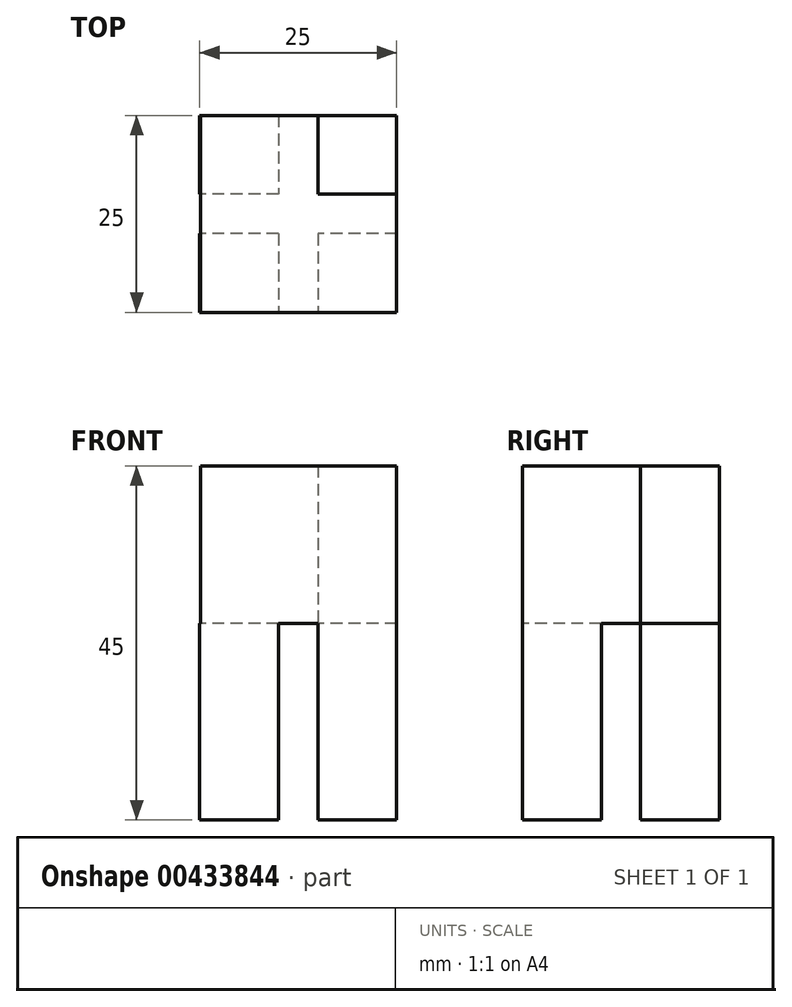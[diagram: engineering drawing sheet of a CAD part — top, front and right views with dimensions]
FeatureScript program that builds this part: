
annotation { "Feature Type Name" : "Feature", "Feature Type Description" : "" }
export const myFeature = defineFeature(function(context is Context, id is Id, definition is map)
    precondition{}
    {
        {
            var Q0;
            Q0=qCreatedBy(makeId("Top.planeOp"),FACE);
            var sketch = newSketch(context, id + "F0", { "sketchPlane" : qUnion([Q0])});
            skLineSegment(sketch, "E0.bottom", {"start": v(0, 0) * mm, "end": v(-10, 0) * mm});
            skLineSegment(sketch, "E0.top", {"start": v(0, -10) * mm, "end": v(-10, -10) * mm});
            skLineSegment(sketch, "E0.left", {"start": v(0, 0) * mm, "end": v(0, -10) * mm});
            skLineSegment(sketch, "E0.right", {"start": v(-10, 0) * mm, "end": v(-10, -10) * mm});
            skLineSegment(sketch, "E1.0.1.0", {"start": v(0, 15) * mm, "end": v(-10, 15) * mm});
            skLineSegment(sketch, "E1.0.1.1", {"start": v(-10, 15) * mm, "end": v(-10, 5) * mm});
            skLineSegment(sketch, "E1.0.1.2", {"start": v(0, 5) * mm, "end": v(-10, 5) * mm});
            skLineSegment(sketch, "E1.0.1.3", {"start": v(0, 15) * mm, "end": v(0, 5) * mm});
            skLineSegment(sketch, "E1.1.0.0", {"start": v(15, 0) * mm, "end": v(5, 0) * mm});
            skLineSegment(sketch, "E1.1.0.1", {"start": v(5, 0) * mm, "end": v(5, -10) * mm});
            skLineSegment(sketch, "E1.1.0.2", {"start": v(15, -10) * mm, "end": v(5, -10) * mm});
            skLineSegment(sketch, "E1.1.0.3", {"start": v(15, 0) * mm, "end": v(15, -10) * mm});
            skLineSegment(sketch, "E1.1.1.0", {"start": v(15, 15) * mm, "end": v(5, 15) * mm});
            skLineSegment(sketch, "E1.1.1.1", {"start": v(5, 15) * mm, "end": v(5, 5) * mm});
            skLineSegment(sketch, "E1.1.1.2", {"start": v(15, 5) * mm, "end": v(5, 5) * mm});
            skLineSegment(sketch, "E1.1.1.3", {"start": v(15, 15) * mm, "end": v(15, 5) * mm});
            skLineSegment(sketch, "E1.direction1", {"start": v(-10, 0) * mm, "end": v(5, 0) * mm, "construction": true});
            skLineSegment(sketch, "E1.direction2", {"start": v(-10, 0) * mm, "end": v(-10, 15) * mm, "construction": true});
            skSolve(sketch);
        }
        {
            var Q0;
            Q0=makeQuery(id+"F0.imprint","IMPRINT",FACE,{"disambiguationData":[TD([[makeQuery(id+"F0.imprint","IMPRINT",EDGE,{"derivedFrom":sQuery(id+"F0.wireOp",EDGE,"E0.bottom")}),1.0]])]});
            var Q1;
            Q1=makeQuery(id+"F0.imprint","IMPRINT",FACE,{"disambiguationData":[TD([[makeQuery(id+"F0.imprint","IMPRINT",EDGE,{"derivedFrom":sQuery(id+"F0.wireOp",EDGE,"E1.1.1.0")}),1.0]])]});
            var Q2;
            Q2=makeQuery(id+"F0.imprint","IMPRINT",FACE,{"disambiguationData":[TD([[makeQuery(id+"F0.imprint","IMPRINT",EDGE,{"derivedFrom":sQuery(id+"F0.wireOp",EDGE,"E1.1.0.0")}),1.0]])]});
            var Q3;
            Q3=makeQuery(id+"F0.imprint","IMPRINT",FACE,{"disambiguationData":[TD([[makeQuery(id+"F0.imprint","IMPRINT",EDGE,{"derivedFrom":sQuery(id+"F0.wireOp",EDGE,"E1.0.1.0")}),1.0]])]});
            extrude(context, id + "F1", {"entities" : qUnion([Q0, Q1, Q2, Q3]), "depth" : 25 * mm});
        }
        {
            var Q0;
            Q0=makeQuery(id+"F1.opExtrude","CAP_FACE",FACE,{"disambiguationData":[OSD([sQuery(id+"F0.wireOp",EDGE,"E1.1.1.0"),sQuery(id+"F0.wireOp",EDGE,"E1.1.1.1"),sQuery(id+"F0.wireOp",EDGE,"E1.1.1.2"),sQuery(id+"F0.wireOp",EDGE,"E1.1.1.3")])],"isStart":false});
            var sketch = newSketch(context, id + "F2", { "sketchPlane" : qUnion([Q0])});
            skLineSegment(sketch, "E2.bottom", {"start": v(15, 15) * mm, "end": v(-9.9, 15) * mm});
            skLineSegment(sketch, "E2.top", {"start": v(15, -10) * mm, "end": v(-9.9, -10) * mm});
            skLineSegment(sketch, "E2.left", {"start": v(15, 15) * mm, "end": v(15, -10) * mm});
            skLineSegment(sketch, "E2.right", {"start": v(-9.9, 15) * mm, "end": v(-9.9, -10) * mm});
            skSolve(sketch);
        }
        {
            var Q0;
            Q0 = qSketchRegion(id + "F0", true);
            var Q1;
            {var subQ3=sQuery(id+"F2.wireOp",EDGE,"E2.top");Q1=makeQuery(id+"F2.imprint","IMPRINT",FACE,{"disambiguationData":[TD([[makeQuery(id+"F2.imprint","IMPRINT",EDGE,{"derivedFrom":subQ3}),-1.0]])]});}
            extrude(context, id + "F3", {"entities" : qUnion([Q0, Q1]), "operationType" : NewBodyOperationType.ADD, "depth" : 20 * mm});
        }
    });
